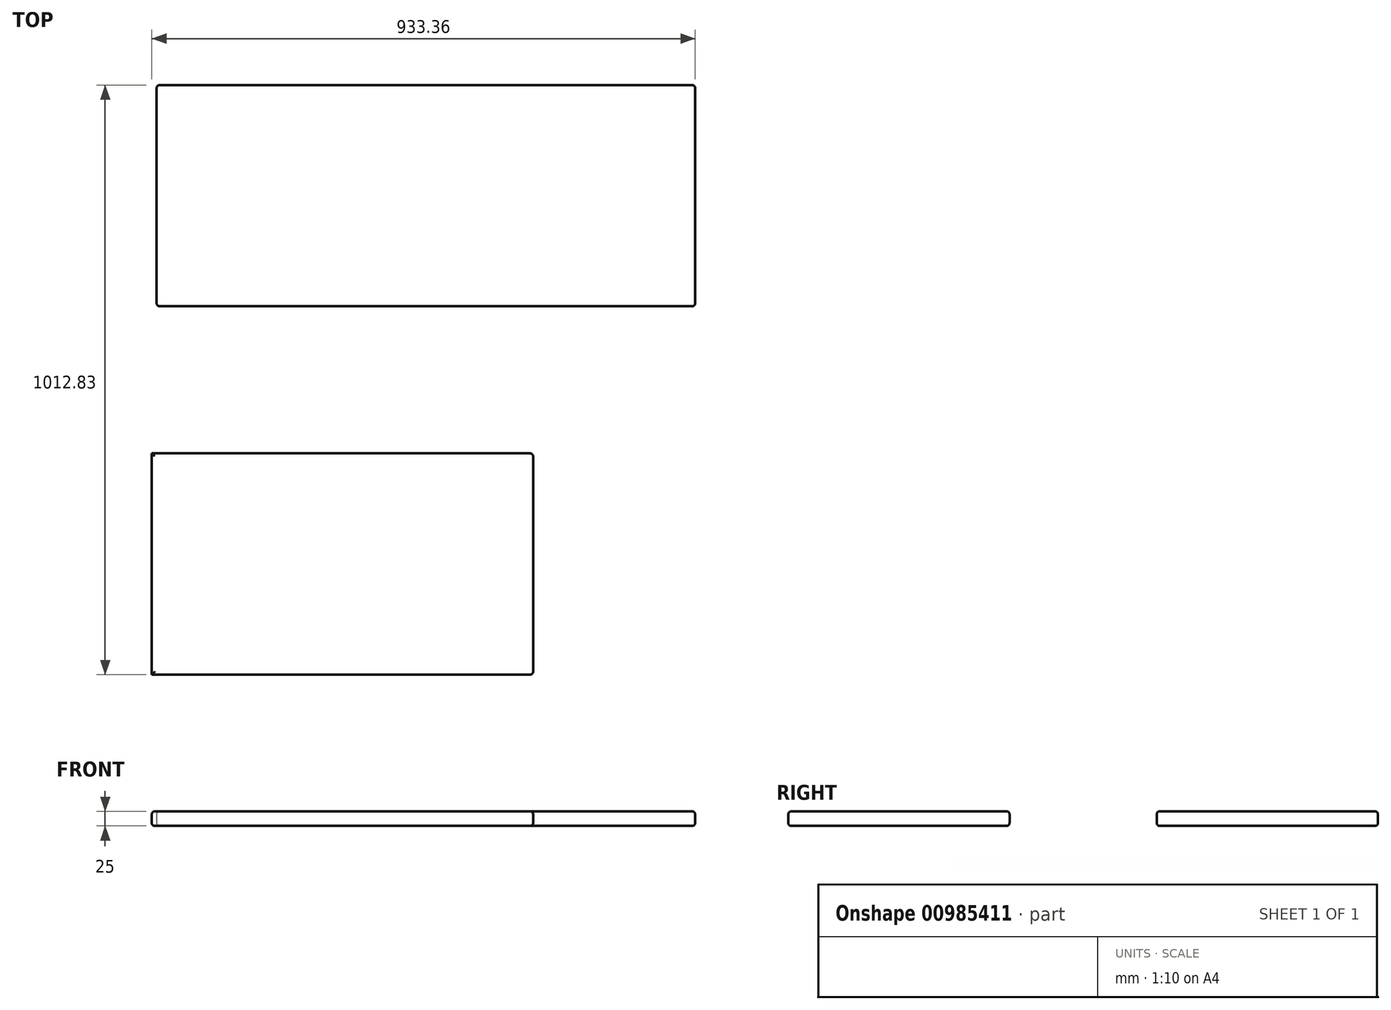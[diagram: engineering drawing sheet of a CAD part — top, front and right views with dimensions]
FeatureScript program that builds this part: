
annotation { "Feature Type Name" : "Feature", "Feature Type Description" : "" }
export const myFeature = defineFeature(function(context is Context, id is Id, definition is map)
    precondition{}
    {
        {
            var Q0;
            Q0=qCreatedBy(makeId("Top.planeOp"),FACE);
            var sketch = newSketch(context, id + "F0", { "sketchPlane" : qUnion([Q0])});
            skLineSegment(sketch, "E0.bottom", {"start": v(-280.96, -860.1) * mm, "end": v(374.04, -860.1) * mm});
            skLineSegment(sketch, "E0.top", {"start": v(-280.96, -480.1) * mm, "end": v(374.04, -480.1) * mm});
            skLineSegment(sketch, "E0.left", {"start": v(-280.96, -860.1) * mm, "end": v(-280.96, -480.1) * mm});
            skLineSegment(sketch, "E0.right", {"start": v(374.04, -860.1) * mm, "end": v(374.04, -480.1) * mm});
            skSolve(sketch);
        }
        {
            var Q0;
            Q0=makeQuery(id+"F0.imprint","IMPRINT",FACE,{"disambiguationData":[TD([[makeQuery(id+"F0.imprint","IMPRINT",EDGE,{"derivedFrom":sQuery(id+"F0.wireOp",EDGE,"E0.bottom")}),1.0]])]});
            extrude(context, id + "F1", {"entities" : qUnion([Q0]), "depth" : 25 * mm, "offsetDistance" : 25 * mm});
        }
        {
            var Q0;
            Q0=makeQuery(id+"F1.opExtrude","SWEPT_FACE",FACE,{"disambiguationData":[OSD([sQuery(id+"F0.wireOp",EDGE,"E0.bottom")])]});
            var sketch = newSketch(context, id + "F2", { "sketchPlane" : qUnion([Q0])});
            skLineSegment(sketch, "E1", {"start": v(-321.2, 5.02) * mm, "end": v(-293.83, 27.9) * mm});
            skLineSegment(sketch, "E2", {"start": v(-293.83, 27.9) * mm, "end": v(-329.54, 27.9) * mm});
            skLineSegment(sketch, "E3", {"start": v(-329.54, 27.9) * mm, "end": v(-329.54, 5.02) * mm});
            skLineSegment(sketch, "E4", {"start": v(-329.54, 5.02) * mm, "end": v(-321.2, 5.02) * mm});
            skSolve(sketch);
        }
        {
            var Q0;
            {var subQ0=sQuery(id+"F2.wireOp",EDGE,"E2");Q0=makeQuery(id+"F2.imprint","IMPRINT",FACE,{"disambiguationData":[TD([[makeQuery(id+"F2.imprint","IMPRINT",EDGE,{"derivedFrom":subQ0}),1.0]])]});}
            var Q1;
            {var subQ0=sQuery(id+"F2.wireOp",EDGE,"E1");var subQ1=sQuery(id+"F0.wireOp",EDGE,"E0.bottom");var subQ2=makeQuery(id+"F1.opExtrude","SWEPT_FACE",FACE,{"disambiguationData":[OSD([subQ1])]});var subQ5=makeQuery(id+"FveuOzHVHpdo9ir_1.opFillet","BLEND_EDGE",EDGE,{"blendedFrom":[makeQuery(id+"F1.opExtrude","CAP_EDGE",EDGE,{"disambiguationData":[OSD([subQ1])],"isStart":false}),subQ2],"blendedInto":[subQ2]});var subQ6=makeQuery(id+"F2.imprint","INTERSECT",VERTEX,{"derivedFrom":[subQ5,subQ0]});Q1=makeQuery(id+"F2.imprint","IMPRINT",FACE,{"disambiguationData":[TD([[makeQuery(id+"F2.imprint","IMPRINT",EDGE,{"disambiguationData":[TD([[subQ6,1.0]])],"derivedFrom":subQ0}),1.0]])]});}
            extrude(context, id + "F3", {"entities" : qUnion([Q0, Q1]), "operationType" : NewBodyOperationType.REMOVE, "endBound" : BoundingType.THROUGH_ALL, "oppositeDirection" : true, "depth" : 25 * mm, "offsetDistance" : 25 * mm});
        }
        {
            var Q0;
            Q0=makeQuery(id+"F1.opExtrude","CAP_FACE",FACE,{"disambiguationData":[OSD([sQuery(id+"F0.wireOp",EDGE,"E0.bottom"),sQuery(id+"F0.wireOp",EDGE,"E0.top"),sQuery(id+"F0.wireOp",EDGE,"E0.left"),sQuery(id+"F0.wireOp",EDGE,"E0.right")])],"isStart":false});
            var Q1;
            Q1=makeQuery(id+"F1.opExtrude","CAP_FACE",FACE,{"disambiguationData":[OSD([sQuery(id+"F0.wireOp",EDGE,"E0.bottom"),sQuery(id+"F0.wireOp",EDGE,"E0.top"),sQuery(id+"F0.wireOp",EDGE,"E0.left"),sQuery(id+"F0.wireOp",EDGE,"E0.right")])],"isStart":true});
            var Q2;
            Q2=makeQuery(id+"F3.boolean.opBoolean","INTERSECT",EDGE,{"derivedFrom":[makeQuery(id+"F1.opExtrude","SWEPT_FACE",FACE,{"disambiguationData":[OSD([sQuery(id+"F0.wireOp",EDGE,"E0.top")])]}),makeQuery(id+"F3.opExtrude","SWEPT_FACE",FACE,{"disambiguationData":[OSD([sQuery(id+"F2.wireOp",EDGE,"E1")])]})]});
            var Q3;
            Q3=makeQuery(id+"F3.boolean.opBoolean","COPY",EDGE,{"derivedFrom":makeQuery(id+"F3.opExtrude","CAP_EDGE",EDGE,{"disambiguationData":[OSD([sQuery(id+"F2.wireOp",EDGE,"E1")])],"isStart":true})});
            var Q4;
            Q4=makeQuery(id+"F1.opExtrude","SWEPT_EDGE",EDGE,{"disambiguationData":[OSD([sQuery(id+"F0.wireOp",EDGE,"E0.bottom"),sQuery(id+"F0.wireOp",EDGE,"E0.right")])]});
            var Q5;
            Q5=makeQuery(id+"F1.opExtrude","SWEPT_EDGE",EDGE,{"disambiguationData":[OSD([sQuery(id+"F0.wireOp",EDGE,"E0.top"),sQuery(id+"F0.wireOp",EDGE,"E0.right")])]});
            fillet(context, id + "F4", {"entities" : qUnion([Q0, Q1, Q2, Q3, Q4, Q5]), "radius" : 5 * mm, "tangentPropagation" : true, "allowEdgeOverflow" : false});
        }
        {
            var Q0;
            Q0=qCreatedBy(makeId("Top.planeOp"),FACE);
            var sketch = newSketch(context, id + "F5", { "sketchPlane" : qUnion([Q0])});
            skLineSegment(sketch, "E5.bottom", {"start": v(652.4, 152.73) * mm, "end": v(-272.6, 152.73) * mm});
            skLineSegment(sketch, "E5.top", {"start": v(652.4, -227.27) * mm, "end": v(-272.6, -227.27) * mm});
            skLineSegment(sketch, "E5.left", {"start": v(652.4, 152.73) * mm, "end": v(652.4, -227.27) * mm});
            skLineSegment(sketch, "E5.right", {"start": v(-272.6, 152.73) * mm, "end": v(-272.6, -227.27) * mm});
            skSolve(sketch);
        }
        {
            var Q0;
            Q0=makeQuery(id+"F5.imprint","IMPRINT",FACE,{"disambiguationData":[TD([[makeQuery(id+"F5.imprint","IMPRINT",EDGE,{"derivedFrom":sQuery(id+"F5.wireOp",EDGE,"E5.bottom")}),1.0]])]});
            extrude(context, id + "F6", {"entities" : qUnion([Q0]), "depth" : 25 * mm, "offsetDistance" : 25 * mm});
        }
        {
            var Q0;
            Q0=makeQuery(id+"F6.opExtrude","CAP_FACE",FACE,{"disambiguationData":[OSD([sQuery(id+"F5.wireOp",EDGE,"E5.bottom"),sQuery(id+"F5.wireOp",EDGE,"E5.top"),sQuery(id+"F5.wireOp",EDGE,"E5.left"),sQuery(id+"F5.wireOp",EDGE,"E5.right")])],"isStart":false});
            var Q1;
            Q1=makeQuery(id+"F6.opExtrude","CAP_FACE",FACE,{"disambiguationData":[OSD([sQuery(id+"F5.wireOp",EDGE,"E5.bottom"),sQuery(id+"F5.wireOp",EDGE,"E5.top"),sQuery(id+"F5.wireOp",EDGE,"E5.left"),sQuery(id+"F5.wireOp",EDGE,"E5.right")])],"isStart":true});
            var Q2;
            Q2=makeQuery(id+"F6.opExtrude","SWEPT_FACE",FACE,{"disambiguationData":[OSD([sQuery(id+"F5.wireOp",EDGE,"E5.bottom")])]});
            var Q3;
            Q3=makeQuery(id+"F6.opExtrude","SWEPT_FACE",FACE,{"disambiguationData":[OSD([sQuery(id+"F5.wireOp",EDGE,"E5.top")])]});
            fillet(context, id + "F7", {"entities" : qUnion([Q0, Q1, Q2, Q3]), "radius" : 5 * mm, "tangentPropagation" : true, "allowEdgeOverflow" : false});
        }
    });
